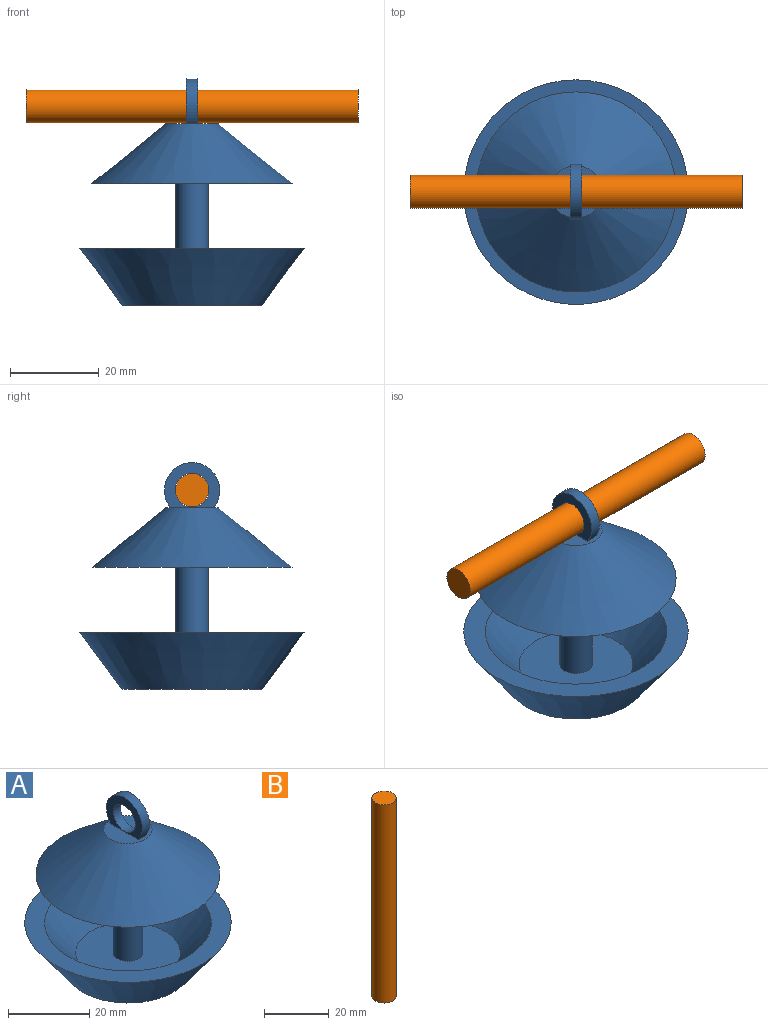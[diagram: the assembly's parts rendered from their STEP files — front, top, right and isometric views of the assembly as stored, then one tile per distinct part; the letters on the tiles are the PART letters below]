
ASSEMBLY  parts=2 mates=1
PART A: 13 faces, bbox 50.7x50.7x51.3 mm
  f0: cylinder r=6.25mm len=12.5mm, axis (-1,0,0), area 70.8mm2, adj f1,f2,f4
  f1: plane 12.5x10.25mm, normal (1,0,0), area 62.3mm2, adj f0,f3,f4
  f2: plane 12.5x10.25mm, normal (-1,0,0), area 62.3mm2, adj f0,f3,f4
  f3: cylinder r=3.8mm len=7.6mm, axis (-1,0,0), area 59.7mm2, adj f1,f2
  f4: plane 11.84x11.84mm, normal (0,0,1), area 86.1mm2, adj f0,f1,f2,f5
  f5: cone r=5.92mm half-angle=51.3deg, axis (0,0,-1), area 1918.6mm2, adj f4,f6
  f6: plane 45.23x45.23mm, normal (0,0,-1), area 1564.5mm2, adj f5,f7
  f7: cylinder r=3.65mm len=23.63mm, axis (0,0,-1), area 542.4mm2, adj f6,f8
  f8: plane 25.73x25.73mm, normal (0,0,1), area 478.1mm2, adj f7,f9
  f9: cone r=12.87mm half-angle=40.3deg, axis (0,0,1), area 1237.1mm2, adj f8,f10
  f10: plane 50.72x50.72mm, normal (0,0,1), area 699.5mm2, adj f9,f11
  f11: cone r=25.36mm half-angle=36.4deg, axis (0,0,1), area 2082.6mm2, adj f10,f12
  f12: plane 31.62x31.62mm, normal (0,0,-1), area 785.3mm2, adj f11
PART B: 3 faces, bbox 7.5x7.5x75 mm
  f0: cylinder r=3.75mm len=75mm, axis (0,0,-1), area 1767.1mm2, adj f1,f2
  f1: plane 7.5x7.5mm, normal (0,0,1), area 44.2mm2, adj f0
  f2: plane 7.5x7.5mm, normal (0,0,-1), area 44.2mm2, adj f0
PLACE A at identity fixed
PLACE B rot(axis=(0,1,0),90deg) t=(-37.5,0,45)mm
MATE revolute A.f3 <-> B.f0  axis (-1,0,0) through (0,0,45)mm
